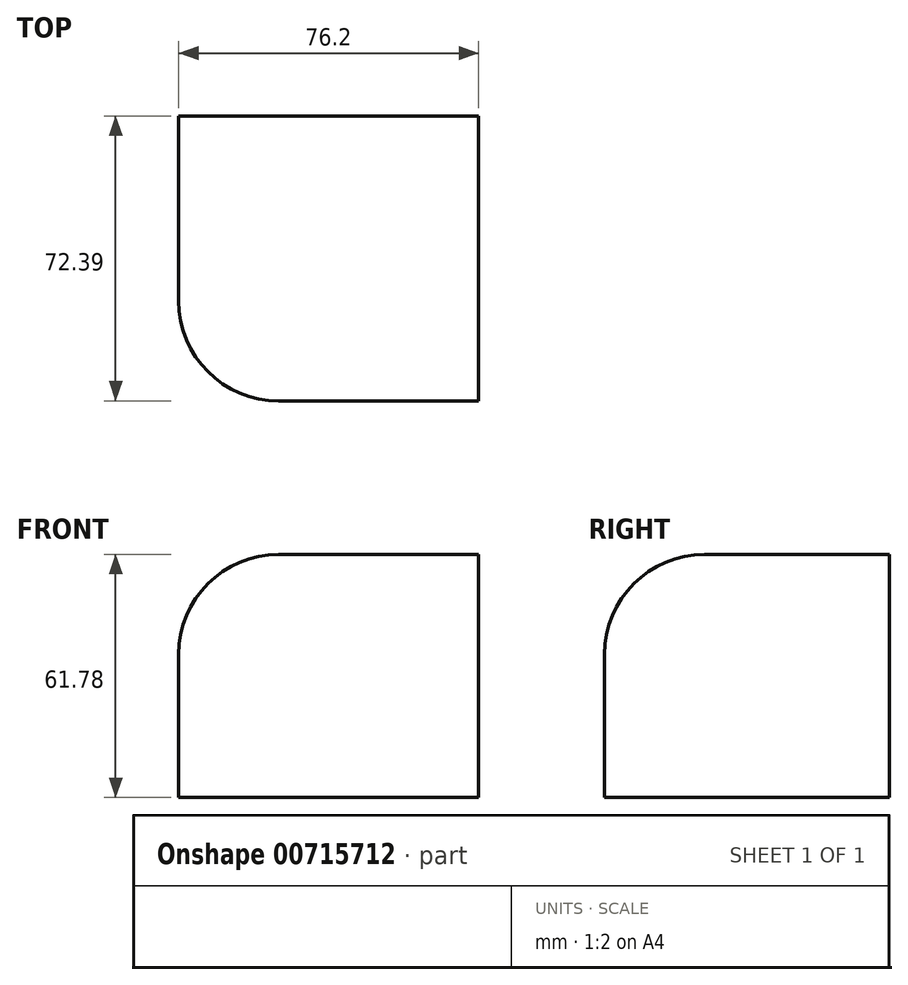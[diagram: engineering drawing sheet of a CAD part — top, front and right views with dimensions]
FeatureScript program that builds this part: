
annotation { "Feature Type Name" : "Feature", "Feature Type Description" : "" }
export const myFeature = defineFeature(function(context is Context, id is Id, definition is map)
    precondition{}
    {
        {
            var Q0;
            Q0=qCreatedBy(makeId("Front.planeOp"),FACE);
            var sketch = newSketch(context, id + "F0", { "sketchPlane" : qUnion([Q0])});
            skLineSegment(sketch, "E0.bottom", {"start": v(-42.77, 31.06) * mm, "end": v(33.43, 31.06) * mm});
            skLineSegment(sketch, "E0.top", {"start": v(-42.77, -30.72) * mm, "end": v(33.43, -30.72) * mm});
            skLineSegment(sketch, "E0.left", {"start": v(-42.77, 31.06) * mm, "end": v(-42.77, -30.72) * mm});
            skLineSegment(sketch, "E0.right", {"start": v(33.43, 31.06) * mm, "end": v(33.43, -30.72) * mm});
            skSolve(sketch);
        }
        {
            var Q0;
            Q0=makeQuery(id+"F0.imprint","IMPRINT",FACE,{"disambiguationData":[TD([[makeQuery(id+"F0.imprint","IMPRINT",EDGE,{"derivedFrom":sQuery(id+"F0.wireOp",EDGE,"E0.bottom")}),-1.0]])]});
            extrude(context, id + "F1", {"entities" : qUnion([Q0]), "depth" : 72.39 * mm, "offsetDistance" : 25.4 * mm});
        }
        {
            var Q0;
            Q0=makeQuery(id+"F1.opExtrude","CAP_EDGE",EDGE,{"disambiguationData":[OSD([sQuery(id+"F0.wireOp",EDGE,"E0.bottom")])],"isStart":false});
            var Q1;
            Q1=makeQuery(id+"F1.opExtrude","SWEPT_EDGE",EDGE,{"disambiguationData":[OSD([sQuery(id+"F0.wireOp",EDGE,"E0.bottom"),sQuery(id+"F0.wireOp",EDGE,"E0.left")])]});
            var Q2;
            Q2=makeQuery(id+"F1.opExtrude","CAP_EDGE",EDGE,{"disambiguationData":[OSD([sQuery(id+"F0.wireOp",EDGE,"E0.left")])],"isStart":false});
            fillet(context, id + "F2", {"entities" : qUnion([Q0, Q1, Q2]), "radius" : 25.4 * mm, "tangentPropagation" : true, "allowEdgeOverflow" : false});
        }
    });
